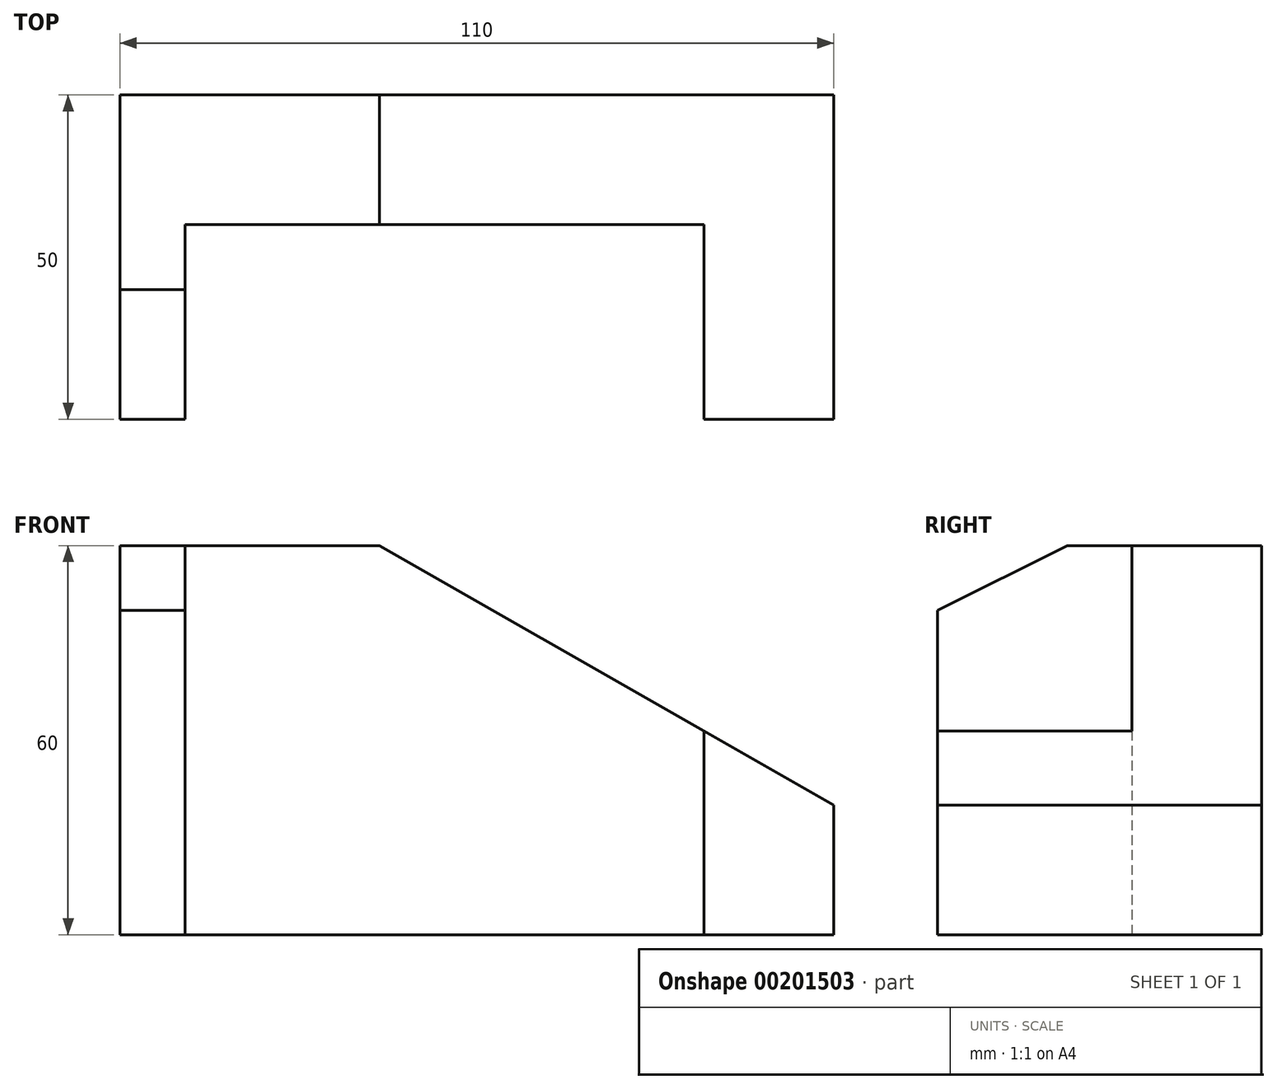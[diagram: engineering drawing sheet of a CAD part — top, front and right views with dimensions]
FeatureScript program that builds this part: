
annotation { "Feature Type Name" : "Feature", "Feature Type Description" : "" }
export const myFeature = defineFeature(function(context is Context, id is Id, definition is map)
    precondition{}
    {
        {
            var Q0;
            Q0=qCreatedBy(makeId("Top.planeOp"),FACE);
            var sketch = newSketch(context, id + "F0", { "sketchPlane" : qUnion([Q0])});
            skLineSegment(sketch, "E0", {"start": v(0, 0) * mm, "end": v(0, 50) * mm});
            skLineSegment(sketch, "E1", {"start": v(0, 50) * mm, "end": v(110, 50) * mm});
            skLineSegment(sketch, "E2", {"start": v(110, 50) * mm, "end": v(110, 0) * mm});
            skLineSegment(sketch, "E3", {"start": v(110, 0) * mm, "end": v(90, 0) * mm});
            skLineSegment(sketch, "E4", {"start": v(90, 0) * mm, "end": v(90, 30) * mm});
            skLineSegment(sketch, "E5", {"start": v(90, 30) * mm, "end": v(10, 30) * mm});
            skLineSegment(sketch, "E6", {"start": v(10, 30) * mm, "end": v(10, 0) * mm});
            skLineSegment(sketch, "E7", {"start": v(10, 0) * mm, "end": v(0, 0) * mm});
            skSolve(sketch);
        }
        {
            var Q0;
            Q0=qSketchRegion(id+"F0",true);
            extrude(context, id + "F1", {"entities" : qUnion([Q0]), "depth" : 60 * mm});
        }
        {
            var Q0;
            Q0=makeQuery(id+"F1.opExtrude","CAP_EDGE",EDGE,{"disambiguationData":[OSD([sQuery(id+"F0.wireOp",EDGE,"E7")])],"isStart":false});
            chamfer(context, id + "F2", {"entities" : qUnion([Q0]), "chamferType" : ChamferType.TWO_OFFSETS, "width1" : 20 * mm, "oppositeDirection" : true, "width2" : 10 * mm, "tangentPropagation" : true});
        }
        {
            var Q0;
            Q0=makeQuery(id+"F1.opExtrude","CAP_EDGE",EDGE,{"disambiguationData":[OSD([sQuery(id+"F0.wireOp",EDGE,"E2")])],"isStart":false});
            chamfer(context, id + "F3", {"entities" : qUnion([Q0]), "chamferType" : ChamferType.TWO_OFFSETS, "width1" : (60 - 20) * mm, "oppositeDirection" : false, "width2" : (110 - 40) * mm, "tangentPropagation" : true});
        }
    });
